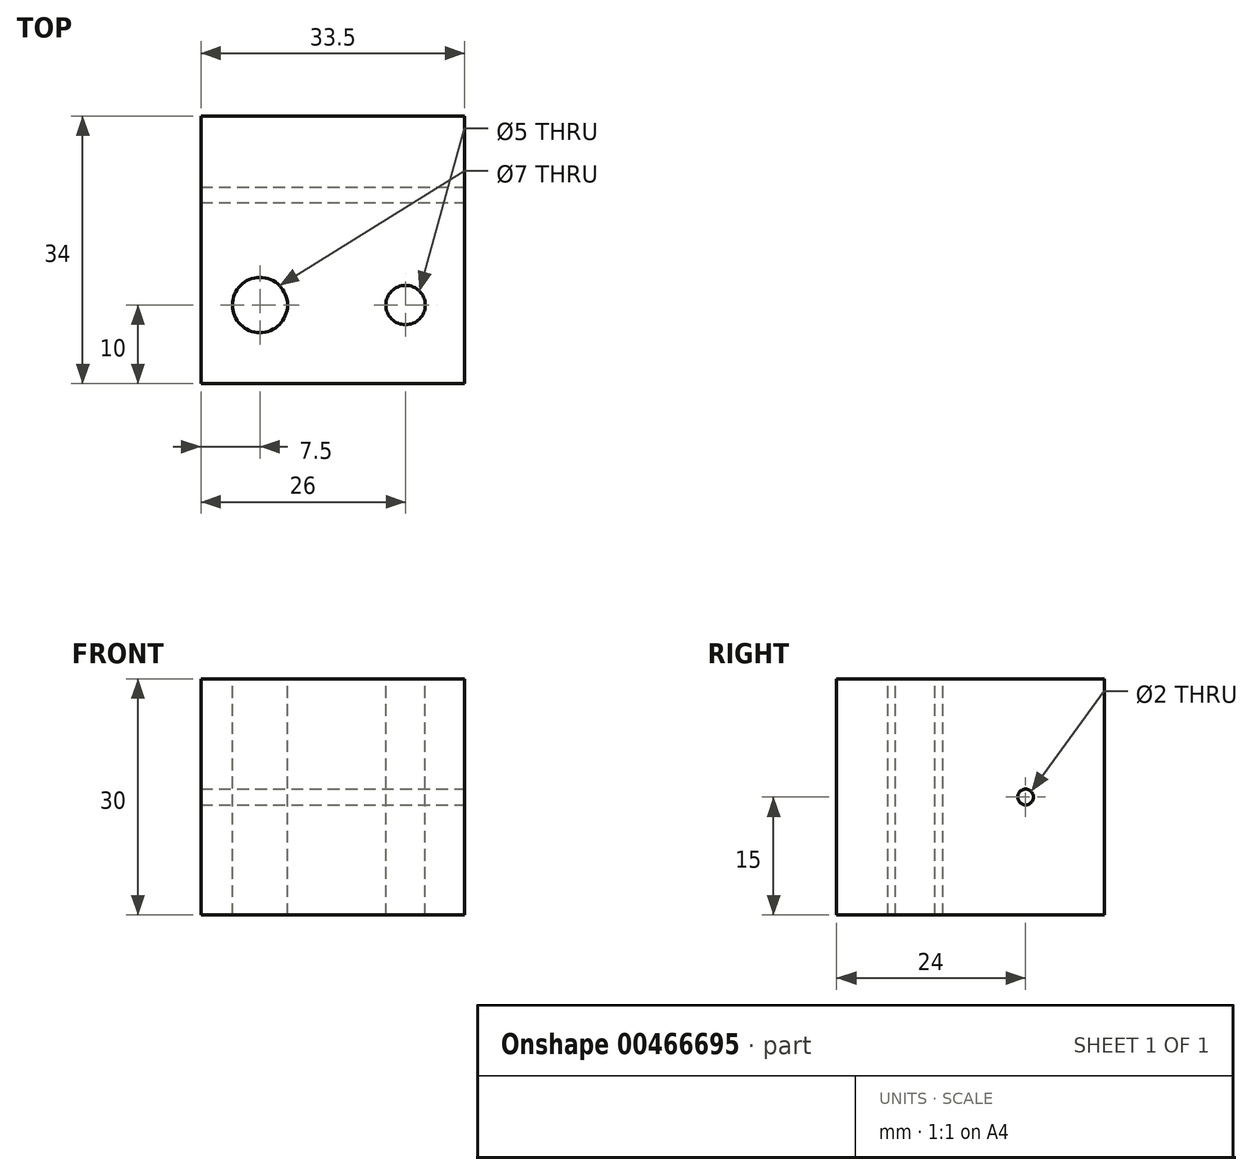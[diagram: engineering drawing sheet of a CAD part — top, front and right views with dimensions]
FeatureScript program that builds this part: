
annotation { "Feature Type Name" : "Feature", "Feature Type Description" : "" }
export const myFeature = defineFeature(function(context is Context, id is Id, definition is map)
    precondition{}
    {
        {
            var Q0;
            Q0=qCreatedBy(makeId("Top.planeOp"),FACE);
            var sketch = newSketch(context, id + "F0", { "sketchPlane" : qUnion([Q0])});
            skLineSegment(sketch, "E0.bottom", {"start": v(-16.75, 10) * mm, "end": v(16.75, 10) * mm});
            skLineSegment(sketch, "E0.top", {"start": v(-16.75, -10) * mm, "end": v(16.75, -10) * mm});
            skLineSegment(sketch, "E0.left", {"start": v(-16.75, 10) * mm, "end": v(-16.75, -10) * mm});
            skLineSegment(sketch, "E0.right", {"start": v(16.75, 10) * mm, "end": v(16.75, -10) * mm});
            skPoint(sketch, "E0.middle", {"position": v(0, 0) * mm});
            skSolve(sketch);
        }
        {
            var Q0;
            Q0=qSketchRegion(id+"F0",true);
            extrude(context, id + "F1", {"entities" : qUnion([Q0]), "depth" : 30 * mm});
        }
        {
            var Q0;
            Q0=makeQuery(id+"F1.opExtrude","CAP_FACE",FACE,{"disambiguationData":[OSD([sQuery(id+"F0.wireOp",EDGE,"E0.bottom"),sQuery(id+"F0.wireOp",EDGE,"E0.top"),sQuery(id+"F0.wireOp",EDGE,"E0.left"),sQuery(id+"F0.wireOp",EDGE,"E0.right")])],"isStart":false});
            var sketch = newSketch(context, id + "F2", { "sketchPlane" : qUnion([Q0])});
            skPoint(sketch, "E1", {"position": v(9.25, 0) * mm});
            skPoint(sketch, "E2", {"position": v(-9.25, 0) * mm});
            skSolve(sketch);
        }
        {
            var Q0;
            Q0=sQuery(id+"F2.wireOp",VERTEX,"E1");
            var Q1;
            Q1=makeQuery(id+"F1.opExtrude","SWEPT_BODY",BODY,{"disambiguationData":[OSD([sQuery(id+"F0.wireOp",EDGE,"E0.bottom"),sQuery(id+"F0.wireOp",EDGE,"E0.top"),sQuery(id+"F0.wireOp",EDGE,"E0.left"),sQuery(id+"F0.wireOp",EDGE,"E0.right")])]});
            hole(context, id + "F3", {"style" : HoleStyle.SIMPLE, "endStyle" : HoleEndStyle.THROUGH, "holeDiameter" : 5 * mm, "isTappedThrough" : true, "tappedDepth" : 12 * mm, "tapClearance" : 3, "locations" : qUnion([Q0]), "scope" : qUnion([Q1])});
        }
        {
            var Q0;
            Q0=sQuery(id+"F2.wireOp",VERTEX,"E2");
            var Q1;
            Q1=makeQuery(id+"F1.opExtrude","SWEPT_BODY",BODY,{"disambiguationData":[OSD([sQuery(id+"F0.wireOp",EDGE,"E0.bottom"),sQuery(id+"F0.wireOp",EDGE,"E0.top"),sQuery(id+"F0.wireOp",EDGE,"E0.left"),sQuery(id+"F0.wireOp",EDGE,"E0.right")])]});
            hole(context, id + "F4", {"style" : HoleStyle.SIMPLE, "endStyle" : HoleEndStyle.THROUGH, "holeDiameter" : 7 * mm, "isTappedThrough" : true, "tappedDepth" : 12 * mm, "tapClearance" : 3, "locations" : qUnion([Q0]), "scope" : qUnion([Q1])});
        }
        {
            var Q0;
            Q0=qCreatedBy(makeId("Top.planeOp"),FACE);
            var sketch = newSketch(context, id + "F5", { "sketchPlane" : qUnion([Q0])});
            skLineSegment(sketch, "E3.bottom", {"start": v(-16.75, 10) * mm, "end": v(16.75, 10) * mm});
            skLineSegment(sketch, "E3.top", {"start": v(-16.75, 24) * mm, "end": v(16.75, 24) * mm});
            skLineSegment(sketch, "E3.left", {"start": v(-16.75, 10) * mm, "end": v(-16.75, 24) * mm});
            skLineSegment(sketch, "E3.right", {"start": v(16.75, 10) * mm, "end": v(16.75, 24) * mm});
            skSolve(sketch);
        }
        {
            var Q0;
            Q0=makeQuery(id+"F5.imprint","IMPRINT",FACE,{"disambiguationData":[TD([[makeQuery(id+"F5.imprint","IMPRINT",EDGE,{"derivedFrom":sQuery(id+"F5.wireOp",EDGE,"E3.bottom")}),1.0]])]});
            extrude(context, id + "F6", {"entities" : qUnion([Q0]), "operationType" : NewBodyOperationType.ADD, "depth" : 30 * mm});
        }
        {
            var Q0;
            Q0=makeQuery(id+"F6.boolean.opBoolean","MERGE",FACE,{"derivedFrom":[makeQuery(id+"F1.opExtrude","SWEPT_FACE",FACE,{"disambiguationData":[OSD([sQuery(id+"F0.wireOp",EDGE,"E0.right")])]}),makeQuery(id+"F6.opExtrude","SWEPT_FACE",FACE,{"disambiguationData":[OSD([sQuery(id+"F5.wireOp",EDGE,"E3.right")])]})]});
            var sketch = newSketch(context, id + "F7", { "sketchPlane" : qUnion([Q0])});
            skPoint(sketch, "E4", {"position": v(14, 15) * mm});
            skSolve(sketch);
        }
        {
            var Q0;
            Q0=sQuery(id+"F7.wireOp",VERTEX,"E4");
            var Q1;
            Q1=makeQuery(id+"F1.opExtrude","SWEPT_BODY",BODY,{"disambiguationData":[OSD([sQuery(id+"F0.wireOp",EDGE,"E0.bottom"),sQuery(id+"F0.wireOp",EDGE,"E0.top"),sQuery(id+"F0.wireOp",EDGE,"E0.left"),sQuery(id+"F0.wireOp",EDGE,"E0.right")])]});
            hole(context, id + "F8", {"style" : HoleStyle.SIMPLE, "endStyle" : HoleEndStyle.THROUGH, "holeDiameter" : 2 * mm, "isTappedThrough" : true, "tappedDepth" : 12 * mm, "tapClearance" : 3, "locations" : qUnion([Q0]), "scope" : qUnion([Q1])});
        }
    });
